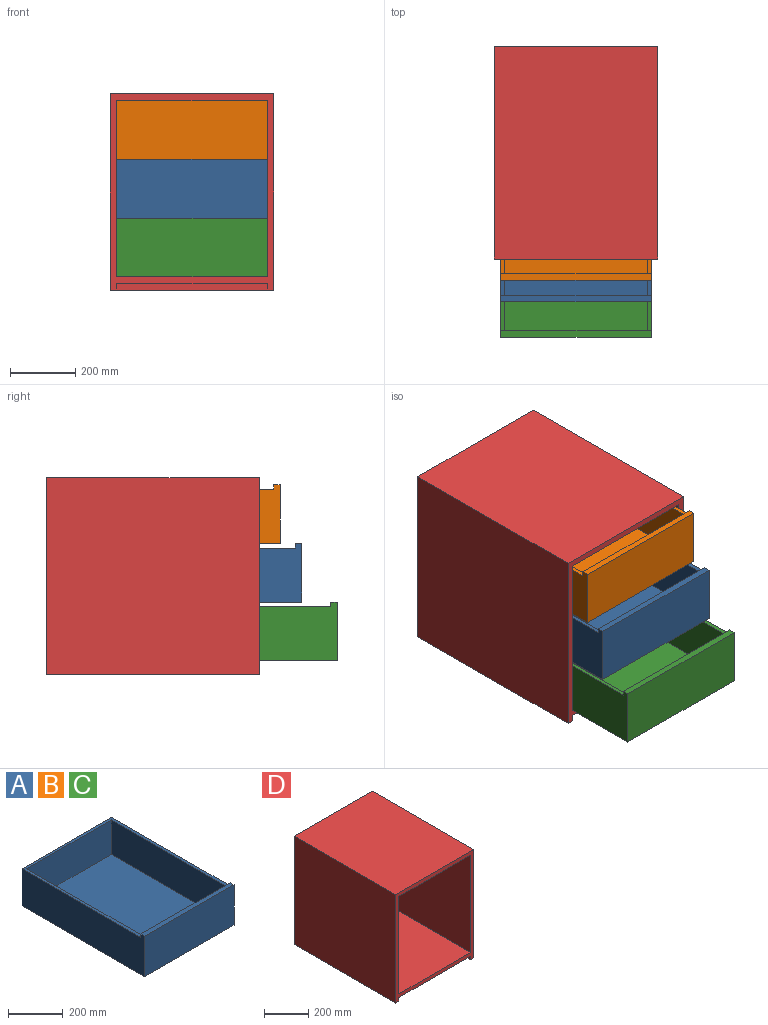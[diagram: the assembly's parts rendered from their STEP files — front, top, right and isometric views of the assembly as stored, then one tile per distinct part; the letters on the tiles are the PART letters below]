
ASSEMBLY  parts=4 mates=3
PART A: 12 faces, bbox 460x632x180 mm
  f0: plane 460x20mm, normal (0,0,1), area 9200mm2, adj f1,f3,f4,f5
  f1: plane 632x180mm, normal (-1,0,0), area 104757.5mm2, adj f0,f2,f4,f5,f6,f10
  f2: plane 632x460mm, normal (0,0,-1), area 290720mm2, adj f1,f3,f5,f10
  f3: plane 632x180mm, normal (1,0,0), area 104757.5mm2, adj f0,f2,f4,f5,f6,f10
  f4: plane 460x168mm, normal (0,1,0), area 73601mm2, adj f0,f1,f3,f6,f7,f8,f9
  f5: plane 460x180mm, normal (0,-1,0), area 82800mm2, adj f0,f1,f2,f3
  f6: plane 612x460mm, normal (0,0,1), area 19920mm2, adj f1,f3,f4,f7,f9,f10,f11
  f7: plane 600x153.29mm, normal (1,0,0), area 91974mm2, adj f4,f6,f8,f11
  f8: plane 600x436mm, normal (0,0,1), area 261600mm2, adj f4,f7,f9,f11
  f9: plane 600x153.29mm, normal (-1,0,0), area 91974mm2, adj f4,f6,f8,f11
  f10: plane 460x165.29mm, normal (0,1,0), area 76033.4mm2, adj f1,f2,f3,f6
  f11: plane 436x153.29mm, normal (0,-1,0), area 66834.4mm2, adj f6,f7,f8,f9
PART B: same geometry as A
PART C: same geometry as A
PART D: 15 faces, bbox 500x650x600 mm
  f0: plane 630x540mm, normal (1,0,0), area 340200mm2, adj f5,f8,f11,f14
  f1: plane 630x540mm, normal (-1,0,0), area 340200mm2, adj f5,f8,f11,f14
  f2: plane 460x20mm, normal (0,-1,0), area 9200mm2, adj f9,f10,f12,f13
  f3: plane 600x500mm, normal (0,1,0), area 300000mm2, adj f4,f6,f7,f12
  f4: plane 650x600mm, normal (-1,0,0), area 390000mm2, adj f3,f5,f7,f12
  f5: plane 600x500mm, normal (0,-1,0), area 42400mm2, adj f0,f1,f4,f6,f7,f8,f9,f10
  f6: plane 650x600mm, normal (1,0,0), area 390000mm2, adj f3,f5,f7,f12
  f7: plane 650x500mm, normal (0,0,1), area 325000mm2, adj f3,f4,f5,f6
  f8: plane 630x460mm, normal (0,0,-1), area 289800mm2, adj f0,f1,f5,f11
  f9: plane 630x20mm, normal (1,0,0), area 12600mm2, adj f2,f5,f12,f13
  f10: plane 630x20mm, normal (-1,0,0), area 12600mm2, adj f2,f5,f12,f13
  f11: plane 540x460mm, normal (0,-1,0), area 248400mm2, adj f0,f1,f8,f14
  f12: plane 650x500mm, normal (0,0,-1), area 35200mm2, adj f2,f3,f4,f5,f6,f9,f10
  f13: plane 630x460mm, normal (0,0,-1), area 289800mm2, adj f2,f5,f9,f10
  f14: plane 630x460mm, normal (0,0,1), area 289800mm2, adj f0,f1,f5,f11
PLACE A t=(-871.54,112.94,236.82)mm
PLACE B t=(-871.54,179.3,416.82)mm
PLACE C t=(-871.54,4.65,56.82)mm
PLACE D t=(-52.43,243.54,416.82)mm
MATE slider C.f5 <-> D.f5  axis (0,-1,0) through (-281.66,-157.93,56.82)mm
MATE slider B.f5 <-> D.f5  axis (0,-1,0) through (-281.66,16.73,416.82)mm
MATE slider A.f5 <-> D.f5  axis (0,-1,0) through (-281.66,-49.63,236.82)mm
